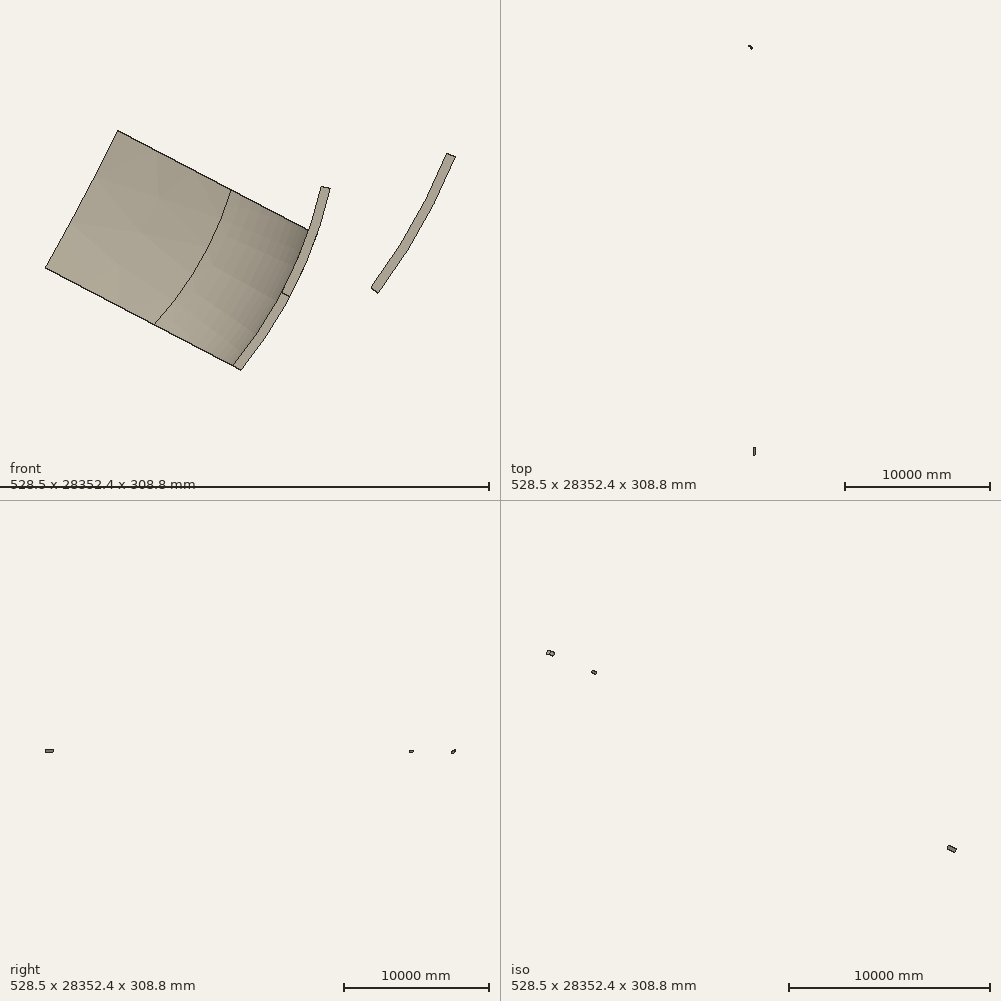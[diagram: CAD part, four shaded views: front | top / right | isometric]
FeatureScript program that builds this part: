
annotation { "Feature Type Name" : "Feature", "Feature Type Description" : "" }
export const myFeature = defineFeature(function(context is Context, id is Id, definition is map)
    precondition{}
    {
        {
            var Q0;
            Q0=qCreatedBy(makeId("Front.planeOp"),FACE);
            var sketch = newSketch(context, id + "F0", { "sketchPlane" : qUnion([Q0])});
            skArc(sketch, "E0", {"start": v(675.9, -351.85) * mm, "mid": v(707.01, -284.22) * mm, "end": v(731.37, -213.87) * mm});
            skArc(sketch, "E1", {"start": v(686.55, -357.4) * mm, "mid": v(718.15, -288.7) * mm, "end": v(742.89, -217.24) * mm});
            skLineSegment(sketch, "E2", {"start": v(0, 0) * mm, "end": v(718.15, -288.7) * mm, "construction": true});
            skLineSegment(sketch, "E3", {"start": v(731.37, -213.87) * mm, "end": v(742.89, -217.24) * mm});
            skLineSegment(sketch, "E4", {"start": v(675.9, -351.85) * mm, "end": v(686.55, -357.4) * mm});
            skSolve(sketch);
        }
        {
            var Q0;
            Q0 = qSketchRegion(id + "F0", true);
            extrude(context, id + "F1", {"entities" : qUnion([Q0]), "oppositeDirection" : true, "depth" : 20000 * mm});
        }
        {
            var Q0;
            Q0=qCreatedBy(makeId("Right.planeOp"),FACE);
            var sketch = newSketch(context, id + "F2", { "sketchPlane" : qUnion([Q0])});
            skLineSegment(sketch, "E5.bottom", {"start": v(0, 0) * mm, "end": v(4100, 0) * mm});
            skLineSegment(sketch, "E5.top", {"start": v(0, -357.4) * mm, "end": v(4100, -357.4) * mm});
            skLineSegment(sketch, "E5.left", {"start": v(0, 0) * mm, "end": v(0, -357.4) * mm});
            skLineSegment(sketch, "E5.right", {"start": v(4100, 0) * mm, "end": v(4100, -357.4) * mm});
            skLineSegment(sketch, "E6.bottom", {"start": v(4400, 0) * mm, "end": v(13100, 0) * mm});
            skLineSegment(sketch, "E6.top", {"start": v(4400, -357.4) * mm, "end": v(13100, -357.4) * mm});
            skLineSegment(sketch, "E6.left", {"start": v(4400, 0) * mm, "end": v(4400, -357.4) * mm});
            skLineSegment(sketch, "E6.right", {"start": v(13100, 0) * mm, "end": v(13100, -357.4) * mm});
            skLineSegment(sketch, "E7.bottom", {"start": v(13400, 0) * mm, "end": v(20000, 0) * mm});
            skLineSegment(sketch, "E7.top", {"start": v(13400, -357.4) * mm, "end": v(20000, -357.4) * mm});
            skLineSegment(sketch, "E7.left", {"start": v(13400, 0) * mm, "end": v(13400, -357.4) * mm});
            skLineSegment(sketch, "E7.right", {"start": v(20000, 0) * mm, "end": v(20000, -357.4) * mm});
            skSolve(sketch);
        }
        {
            var Q0;
            Q0 = qSketchRegion(id + "F2", true);
            extrude(context, id + "F3", {"entities" : qUnion([Q0]), "operationType" : NewBodyOperationType.REMOVE, "endBound" : BoundingType.THROUGH_ALL, "depth" : 25 * mm});
        }
        {
            var Q0;
            Q0=qCreatedBy(makeId("Front.planeOp"),FACE);
            var sketch = newSketch(context, id + "F4", { "sketchPlane" : qUnion([Q0])});
            skArc(sketch, "E8", {"start": v(608.56, -458.58) * mm, "mid": v(663.21, -375.23) * mm, "end": v(706.51, -285.45) * mm});
            skArc(sketch, "E9", {"start": v(618.14, -465.8) * mm, "mid": v(673.66, -381.14) * mm, "end": v(717.64, -289.95) * mm});
            skLineSegment(sketch, "E10", {"start": v(0, 0) * mm, "end": v(673.66, -381.14) * mm, "construction": true});
            skLineSegment(sketch, "E11", {"start": v(706.51, -285.45) * mm, "end": v(717.64, -289.95) * mm});
            skLineSegment(sketch, "E12", {"start": v(608.56, -458.58) * mm, "end": v(618.14, -465.8) * mm});
            skSolve(sketch);
        }
        {
            var Q0;
            Q0 = qSketchRegion(id + "F4", true);
            extrude(context, id + "F5", {"entities" : qUnion([Q0]), "oppositeDirection" : true, "depth" : 20000 * mm});
        }
        {
            var Q0;
            Q0=qCreatedBy(makeId("Right.planeOp"),FACE);
            var sketch = newSketch(context, id + "F6", { "sketchPlane" : qUnion([Q0])});
            skLineSegment(sketch, "E13.bottom", {"start": v(0, 0) * mm, "end": v(3440.7, 0) * mm});
            skLineSegment(sketch, "E13.top", {"start": v(0, -465.8) * mm, "end": v(3440.7, -465.8) * mm});
            skLineSegment(sketch, "E13.left", {"start": v(0, 0) * mm, "end": v(0, -465.8) * mm});
            skLineSegment(sketch, "E13.right", {"start": v(3440.7, 0) * mm, "end": v(3440.7, -465.8) * mm});
            skLineSegment(sketch, "E14.bottom", {"start": v(3990.7, 0) * mm, "end": v(20000, 0) * mm});
            skLineSegment(sketch, "E14.top", {"start": v(3990.7, -465.8) * mm, "end": v(20000, -465.8) * mm});
            skLineSegment(sketch, "E14.left", {"start": v(3990.7, 0) * mm, "end": v(3990.7, -465.8) * mm});
            skLineSegment(sketch, "E14.right", {"start": v(20000, 0) * mm, "end": v(20000, -465.8) * mm});
            skSolve(sketch);
        }
        {
            var Q0;
            Q0 = qSketchRegion(id + "F6", true);
            extrude(context, id + "F7", {"entities" : qUnion([Q0]), "operationType" : NewBodyOperationType.REMOVE, "endBound" : BoundingType.THROUGH_ALL, "depth" : 25 * mm});
        }
        {
            var Q0;
            Q0=sQuery(id+"F0.wireOp",VERTEX,"E2.end");
            var Q1;
            Q1=sQuery(id+"F0.wireOp",EDGE,"E2");
            cPlane(context, id + "F8", {"entities" : qUnion([Q0, Q1]), "cplaneType" : CPlaneType.LINE_POINT, "offset" : 25 * mm, "width" : 150 * mm, "height" : 150 * mm});
        }
        {
            var Q0;
            Q0=qCreatedBy(makeId("Right.planeOp"),FACE);
            var sketch = newSketch(context, id + "F9", { "sketchPlane" : qUnion([Q0])});
            skLineSegment(sketch, "E15", {"start": v(0, 0) * mm, "end": v(2162.82, 0) * mm, "construction": true});
            skSolve(sketch);
        }
        {
            var Q0;
            Q0=sQuery(id+"F4.wireOp",EDGE,"E10");
            var Q1;
            Q1=sQuery(id+"F4.wireOp",VERTEX,"E10.end");
            cPlane(context, id + "F10", {"entities" : qUnion([Q0, Q1]), "cplaneType" : CPlaneType.LINE_POINT, "offset" : 25 * mm, "width" : 150 * mm, "height" : 150 * mm});
        }
        {
            var Q0;
            Q0=qCreatedBy(makeId("Front.planeOp"),FACE);
            cPlane(context, id + "F11", {"entities" : qUnion([Q0]), "cplaneType" : CPlaneType.OFFSET, "offset" : 21500 * mm, "oppositeDirection" : true, "width" : 150 * mm, "height" : 150 * mm});
        }
        {
            var Q0;
            Q0=qCreatedBy(id+"F11.planeOp",FACE);
            var sketch = newSketch(context, id + "F12", { "sketchPlane" : qUnion([Q0])});
            skArc(sketch, "E16", {"start": v(504.45, -470.3) * mm, "mid": v(535, -402.16) * mm, "end": v(556.4, -330.63) * mm});
            skLineSegment(sketch, "E17", {"start": v(0, -203.2) * mm, "end": v(535, -402.16) * mm, "construction": true});
            skArc(sketch, "E18", {"start": v(493.85, -464.68) * mm, "mid": v(523.75, -397.98) * mm, "end": v(544.7, -327.95) * mm});
            skLineSegment(sketch, "E19", {"start": v(544.7, -327.95) * mm, "end": v(556.4, -330.63) * mm});
            skLineSegment(sketch, "E20", {"start": v(493.85, -464.68) * mm, "end": v(504.45, -470.3) * mm});
            skSolve(sketch);
        }
        {
            var Q0;
            Q0 = qSketchRegion(id + "F12", true);
            extrude(context, id + "F13", {"entities" : qUnion([Q0]), "oppositeDirection" : true, "depth" : 10000 * mm});
        }
        {
            var Q0;
            Q0=qCreatedBy(makeId("Right.planeOp"),FACE);
            var sketch = newSketch(context, id + "F14", { "sketchPlane" : qUnion([Q0])});
            skLineSegment(sketch, "E21.bottom", {"start": v(21500, 1931.22) * mm, "end": v(28620, 1931.22) * mm});
            skLineSegment(sketch, "E21.top", {"start": v(21500, -2024.64) * mm, "end": v(28620, -2024.64) * mm});
            skLineSegment(sketch, "E21.left", {"start": v(21500, 1931.22) * mm, "end": v(21500, -2024.64) * mm});
            skLineSegment(sketch, "E21.right", {"start": v(28620, 1931.22) * mm, "end": v(28620, -2024.64) * mm});
            skLineSegment(sketch, "E22.bottom", {"start": v(28920, 1931.22) * mm, "end": v(31500, 1931.22) * mm});
            skLineSegment(sketch, "E22.top", {"start": v(28920, -2024.64) * mm, "end": v(31500, -2024.64) * mm});
            skLineSegment(sketch, "E22.left", {"start": v(28920, 1931.22) * mm, "end": v(28920, -2024.64) * mm});
            skLineSegment(sketch, "E22.right", {"start": v(31500, 1931.22) * mm, "end": v(31500, -2024.64) * mm});
            skSolve(sketch);
        }
        {
            var Q0;
            Q0 = qSketchRegion(id + "F14", true);
            extrude(context, id + "F15", {"entities" : qUnion([Q0]), "operationType" : NewBodyOperationType.REMOVE, "endBound" : BoundingType.THROUGH_ALL, "depth" : 25 * mm});
        }
        {
            var Q0;
            Q0=sQuery(id+"F12.wireOp",EDGE,"E17");
            var Q1;
            Q1=sQuery(id+"F12.wireOp",VERTEX,"E17.end");
            cPlane(context, id + "F16", {"entities" : qUnion([Q0, Q1]), "cplaneType" : CPlaneType.LINE_POINT, "offset" : 25 * mm, "width" : 150 * mm, "height" : 150 * mm});
        }
        {
            var Q0;
            Q0=qCreatedBy(makeId("Right.planeOp"),FACE);
            var sketch = newSketch(context, id + "F17", { "sketchPlane" : qUnion([Q0])});
            skLineSegment(sketch, "E23", {"start": v(31500, 343.6) * mm, "end": v(31535, 343.6) * mm, "construction": true});
            skArc(sketch, "E24", {"start": v(31535, 343.6) * mm, "mid": v(31634.29, 315.4) * mm, "end": v(31703.92, 239.2) * mm, "construction": true});
            skArc(sketch, "E25", {"start": v(31703.92, 239.2) * mm, "mid": v(31781.9, 24.09) * mm, "end": v(31808.37, -203.2) * mm, "construction": true});
            skLineSegment(sketch, "E26", {"start": v(-835.36, -203.2) * mm, "end": v(-88.76, -203.2) * mm, "construction": true});
            skArc(sketch, "E27.0", {"start": v(31714.65, 244.58) * mm, "mid": v(31793.58, 26.84) * mm, "end": v(31820.37, -203.2) * mm, "construction": true});
            skArc(sketch, "E27.1", {"start": v(31535, 355.6) * mm, "mid": v(31640.6, 325.6) * mm, "end": v(31714.65, 244.58) * mm, "construction": true});
            skLineSegment(sketch, "E27.2", {"start": v(31500, 355.6) * mm, "end": v(31535, 355.6) * mm, "construction": true});
            skLineSegment(sketch, "E28", {"start": v(31500, 343.6) * mm, "end": v(31500, 355.6) * mm, "construction": true});
            skLineSegment(sketch, "E29", {"start": v(31808.37, -203.2) * mm, "end": v(31820.37, -203.2) * mm, "construction": true});
            skArc(sketch, "E30.0", {"start": v(31535, 367.6) * mm, "mid": v(31646.9, 335.81) * mm, "end": v(31725.38, 249.94) * mm});
            skArc(sketch, "E31.0", {"start": v(31725.38, 249.94) * mm, "mid": v(31805.26, 29.6) * mm, "end": v(31832.37, -203.2) * mm});
            skLineSegment(sketch, "E32", {"start": v(31535, 367.6) * mm, "end": v(31535, 355.6) * mm});
            skLineSegment(sketch, "E33", {"start": v(31820.37, -203.2) * mm, "end": v(31832.37, -203.2) * mm});
            skArc(sketch, "E34", {"start": v(31714.65, 244.58) * mm, "mid": v(31640.6, 325.6) * mm, "end": v(31535, 355.6) * mm});
            skArc(sketch, "E35", {"start": v(31820.37, -203.2) * mm, "mid": v(31793.58, 26.84) * mm, "end": v(31714.65, 244.58) * mm});
            skSolve(sketch);
        }
        {
            var Q0;
            Q0 = qSketchRegion(id + "F17", true);
            var Q1;
            Q1=sQuery(id+"F17.wireOp",EDGE,"E26");
            revolve(context, id + "F18", {"entities" : qUnion([Q0]), "axis" : qUnion([Q1]), "revolveType" : RevolveType.ONE_DIRECTION, "angle" : 180 * degree});
        }
        {
            var Q0;
            Q0=makeQuery(id+"F18.opRevolve","SWEPT_FACE",FACE,{"disambiguationData":[OSD([sQuery(id+"F17.wireOp",EDGE,"E32")])]});
            var sketch = newSketch(context, id + "F19", { "sketchPlane" : qUnion([Q0])});
            skLineSegment(sketch, "E36", {"start": v(0, -203.2) * mm, "end": v(505.85, -467.65) * mm, "construction": true});
            skLineSegment(sketch, "E37", {"start": v(441.55, -564.93) * mm, "end": v(0, -334.1) * mm});
            skLineSegment(sketch, "E38", {"start": v(0, -334.1) * mm, "end": v(-180.61, -679.58) * mm});
            skLineSegment(sketch, "E39", {"start": v(-180.61, -679.58) * mm, "end": v(260.93, -910.41) * mm});
            skLineSegment(sketch, "E40", {"start": v(260.93, -910.41) * mm, "end": v(441.55, -564.93) * mm});
            skLineSegment(sketch, "E41", {"start": v(-195.44, -6.24) * mm, "end": v(539.25, -390.33) * mm});
            skLineSegment(sketch, "E42", {"start": v(539.25, -390.33) * mm, "end": v(764.79, 41.07) * mm});
            skLineSegment(sketch, "E43", {"start": v(764.79, 41.07) * mm, "end": v(30.1, 425.16) * mm});
            skLineSegment(sketch, "E44", {"start": v(30.1, 425.16) * mm, "end": v(-195.44, -6.24) * mm});
            skSolve(sketch);
        }
        {
            var Q0;
            Q0 = qSketchRegion(id + "F19", true);
            extrude(context, id + "F20", {"entities" : qUnion([Q0]), "operationType" : NewBodyOperationType.REMOVE, "endBound" : BoundingType.THROUGH_ALL, "oppositeDirection" : true, "depth" : 25 * mm});
        }
        {
            var Q0;
            Q0=makeQuery(id+"F20.boolean.opBoolean","COPY",FACE,{"derivedFrom":makeQuery(id+"F20.opExtrude","SWEPT_FACE",FACE,{"disambiguationData":[OSD([sQuery(id+"F19.wireOp",EDGE,"E41")])]})});
            var sketch = newSketch(context, id + "F21", { "sketchPlane" : qUnion([Q0])});
            skLineSegment(sketch, "E45", {"start": v(94.14, 30819.2) * mm, "end": v(415.27, 31939.13) * mm});
            skLineSegment(sketch, "E46", {"start": v(415.27, 31939.13) * mm, "end": v(44.8, 31939.13) * mm});
            skLineSegment(sketch, "E47", {"start": v(44.8, 31939.13) * mm, "end": v(94.14, 30819.2) * mm});
            skLineSegment(sketch, "E48", {"start": v(94.14, 30819.2) * mm, "end": v(94.14, 31268.43) * mm, "construction": true});
            skSolve(sketch);
        }
        {
            var Q0;
            Q0 = qSketchRegion(id + "F21", true);
            extrude(context, id + "F22", {"entities" : qUnion([Q0]), "operationType" : NewBodyOperationType.REMOVE, "endBound" : BoundingType.THROUGH_ALL, "oppositeDirection" : true, "depth" : 25 * mm});
        }
        {
            var Q0;
            Q0=makeQuery(id+"F20.boolean.opBoolean","COPY",FACE,{"derivedFrom":makeQuery(id+"F20.opExtrude","SWEPT_FACE",FACE,{"disambiguationData":[OSD([sQuery(id+"F19.wireOp",EDGE,"E41")])]})});
            var Q1;
            Q1=sQuery(id+"F19.wireOp",VERTEX,"E36.start");
            cPlane(context, id + "F23", {"entities" : qUnion([Q0, Q1]), "cplaneType" : CPlaneType.PLANE_POINT, "offset" : 25 * mm, "width" : 150 * mm, "height" : 150 * mm});
        }
    });
